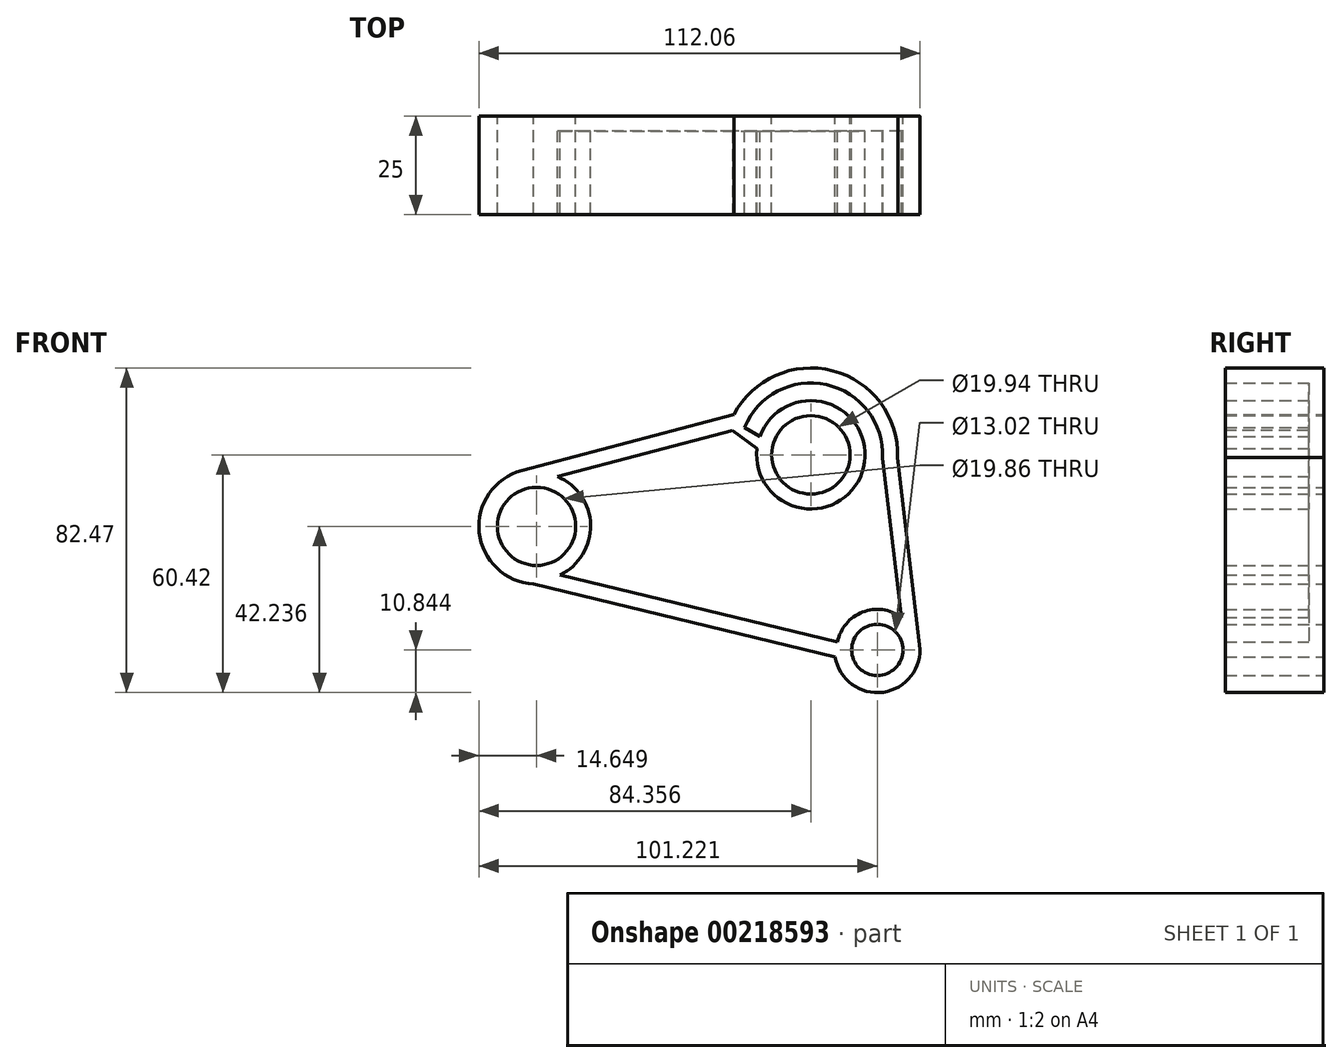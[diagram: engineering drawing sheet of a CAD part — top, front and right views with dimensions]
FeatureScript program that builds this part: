
annotation { "Feature Type Name" : "Feature", "Feature Type Description" : "" }
export const myFeature = defineFeature(function(context is Context, id is Id, definition is map)
    precondition{}
    {
        {
            var Q0;
            Q0=qCreatedBy(makeId("Front.planeOp"),FACE);
            var sketch = newSketch(context, id + "F0", { "sketchPlane" : qUnion([Q0])});
            skCircle(sketch, "E0", {"center": v(-41.78, 18.73) * mm, "radius": 9.93 * mm});
            skCircle(sketch, "E1", {"center": v(-41.78, 18.73) * mm, "radius": 14.65 * mm});
            skCircle(sketch, "E2", {"center": v(44.8, -12.67) * mm, "radius": 10.84 * mm});
            skCircle(sketch, "E3", {"center": v(44.8, -12.67) * mm, "radius": 6.51 * mm});
            skCircle(sketch, "E4", {"center": v(27.93, 36.9) * mm, "radius": 9.97 * mm});
            skCircle(sketch, "E5", {"center": v(27.93, 36.9) * mm, "radius": 22.05 * mm});
            skLineSegment(sketch, "E6", {"start": v(55.56, -11.4) * mm, "end": v(49.97, 36.28) * mm});
            skLineSegment(sketch, "E7", {"start": v(8.37, 47.1) * mm, "end": v(-45.52, 32.9) * mm});
            skLineSegment(sketch, "E8", {"start": v(-47.8, 5.37) * mm, "end": v(34.09, -14.41) * mm});
            skSolve(sketch);
        }
        {
            var Q0;
            Q0 = qSketchRegion(id + "F0", true);
            extrude(context, id + "F1", {"entities" : qUnion([Q0]), "depth" : 25 * mm});
        }
        {
            var Q0;
            Q0=makeQuery(id+"F1.opExtrude","CAP_FACE",FACE,{"disambiguationData":[OSD([sQuery(id+"F0.wireOp",EDGE,"E0"),sQuery(id+"F0.wireOp",EDGE,"E1"),sQuery(id+"F0.wireOp",EDGE,"E2"),sQuery(id+"F0.wireOp",EDGE,"E3"),sQuery(id+"F0.wireOp",EDGE,"E4"),sQuery(id+"F0.wireOp",EDGE,"E5"),sQuery(id+"F0.wireOp",EDGE,"E6"),sQuery(id+"F0.wireOp",EDGE,"E7"),sQuery(id+"F0.wireOp",EDGE,"E8")])],"isStart":false});
            var Q1;
            Q1=makeQuery(id+"F1.opExtrude","SWEPT_BODY",BODY,{"disambiguationData":[OSD([sQuery(id+"F0.wireOp",EDGE,"E0"),sQuery(id+"F0.wireOp",EDGE,"E1"),sQuery(id+"F0.wireOp",EDGE,"E2"),sQuery(id+"F0.wireOp",EDGE,"E3"),sQuery(id+"F0.wireOp",EDGE,"E4"),sQuery(id+"F0.wireOp",EDGE,"E5"),sQuery(id+"F0.wireOp",EDGE,"E6"),sQuery(id+"F0.wireOp",EDGE,"E7"),sQuery(id+"F0.wireOp",EDGE,"E8")])]});
            shell(context, id + "F2", {"entities" : qUnion([Q0]), "parts" : qUnion([Q1]), "thickness" : 3.8 * mm});
        }
        {
            var Q0;
            {var subQ0=sQuery(id+"F0.wireOp",EDGE,"E8");var subQ1=sQuery(id+"F0.wireOp",EDGE,"E7");var subQ2=sQuery(id+"F0.wireOp",EDGE,"E6");var subQ3=sQuery(id+"F0.wireOp",EDGE,"E5");var subQ4=sQuery(id+"F0.wireOp",EDGE,"E4");var subQ5=sQuery(id+"F0.wireOp",EDGE,"E3");var subQ6=sQuery(id+"F0.wireOp",EDGE,"E2");var subQ7=sQuery(id+"F0.wireOp",EDGE,"E1");var subQ8=sQuery(id+"F0.wireOp",EDGE,"E0");Q0=makeQuery(id+"F2.opShell","OFFSET_FACE",FACE,{"disambiguationData":[OSD([subQ8,subQ7,subQ6,subQ5,subQ4,subQ3,subQ2,subQ1,subQ0]),TDD([makeQuery(id+"F1.opExtrude","CAP_FACE",FACE,{"disambiguationData":[OSD([subQ8,subQ7,subQ6,subQ5,subQ4,subQ3,subQ2,subQ1,subQ0])],"isStart":false})])]});}
            var sketch = newSketch(context, id + "F3", { "sketchPlane" : qUnion([Q0])});
            skLineSegment(sketch, "E9", {"start": v(11.06, 43.88) * mm, "end": v(15.19, 41.49) * mm});
            skLineSegment(sketch, "E10", {"start": v(15.19, 41.49) * mm, "end": v(14.37, 38.43) * mm});
            skLineSegment(sketch, "E11", {"start": v(14.37, 38.43) * mm, "end": v(7.56, 43.37) * mm});
            skLineSegment(sketch, "E12", {"start": v(7.56, 43.37) * mm, "end": v(11.06, 43.88) * mm});
            skSolve(sketch);
        }
        {
            var Q0;
            Q0 = qSketchRegion(id + "F3", true);
            var Q1;
            Q1=makeQuery(id+"F1.opExtrude","SWEPT_BODY",BODY,{"disambiguationData":[OSD([sQuery(id+"F0.wireOp",EDGE,"E0"),sQuery(id+"F0.wireOp",EDGE,"E1"),sQuery(id+"F0.wireOp",EDGE,"E2"),sQuery(id+"F0.wireOp",EDGE,"E3"),sQuery(id+"F0.wireOp",EDGE,"E4"),sQuery(id+"F0.wireOp",EDGE,"E5"),sQuery(id+"F0.wireOp",EDGE,"E6"),sQuery(id+"F0.wireOp",EDGE,"E7"),sQuery(id+"F0.wireOp",EDGE,"E8")])]});
            extrude(context, id + "F4", {"entities" : qUnion([Q0]), "operationType" : NewBodyOperationType.ADD, "endBound" : BoundingType.UP_TO_BODY, "oppositeDirection" : true, "endBoundEntityBody" : qUnion([Q1]), "depth" : 25 * mm});
        }
    });
